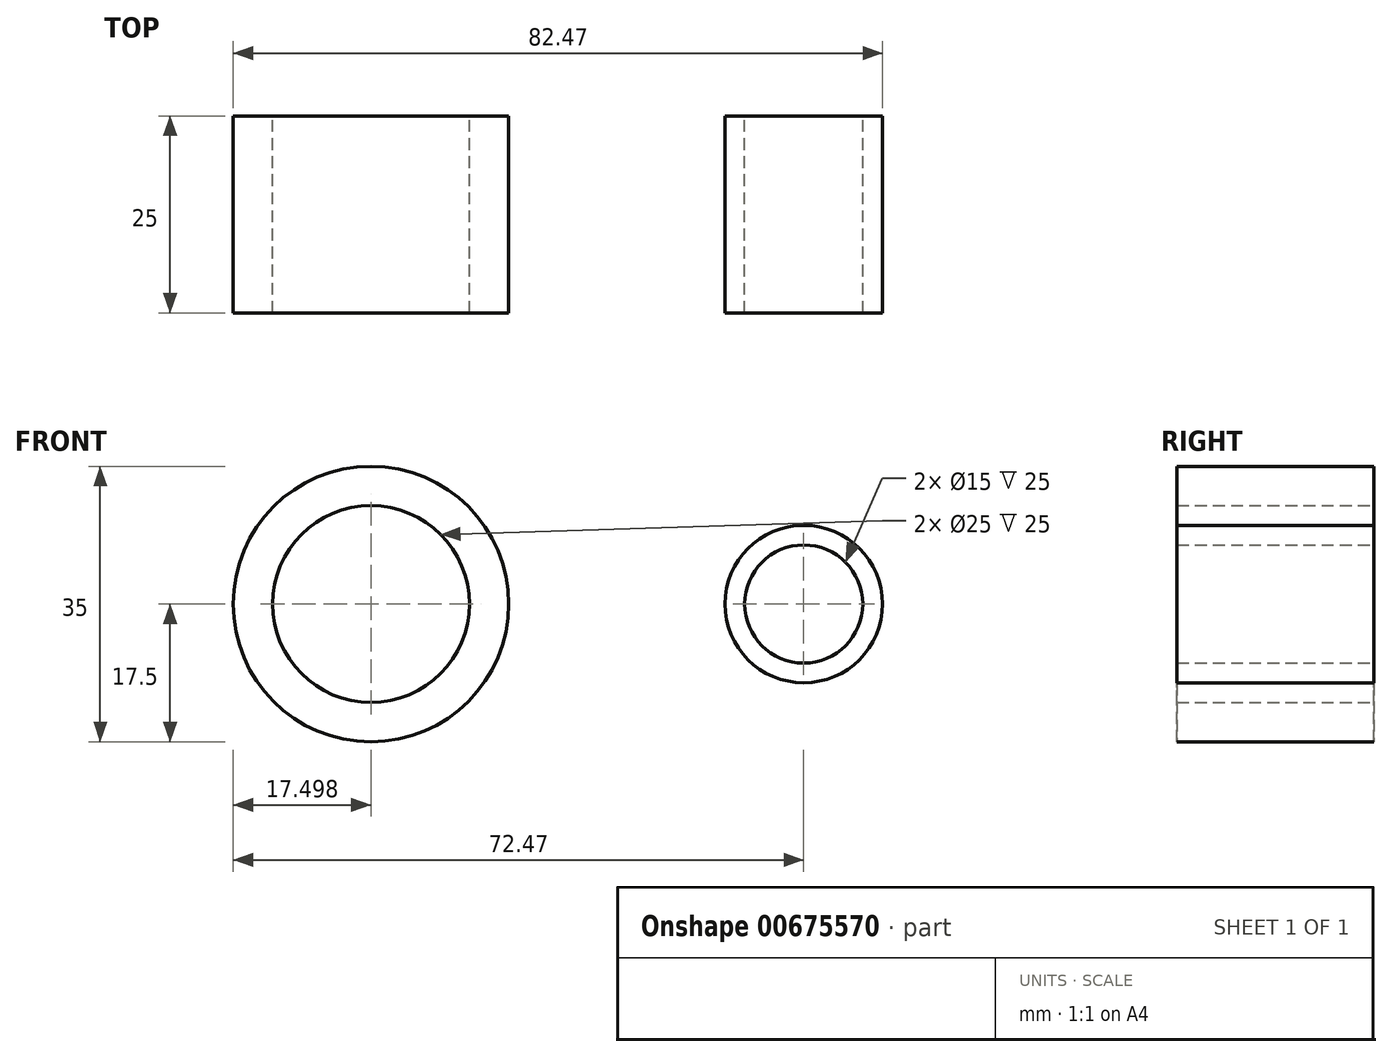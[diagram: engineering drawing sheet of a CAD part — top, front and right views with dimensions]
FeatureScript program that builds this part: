
annotation { "Feature Type Name" : "Feature", "Feature Type Description" : "" }
export const myFeature = defineFeature(function(context is Context, id is Id, definition is map)
    precondition{}
    {
        {
            var Q0;
            Q0=qCreatedBy(makeId("Front.planeOp"),FACE);
            var sketch = newSketch(context, id + "F0", { "sketchPlane" : qUnion([Q0])});
            skCircle(sketch, "E0", {"center": v(-54.97, 0) * mm, "radius": 12.5 * mm});
            skCircle(sketch, "E1", {"center": v(-54.97, 0) * mm, "radius": 17.5 * mm});
            skCircle(sketch, "E2", {"center": v(0, 0) * mm, "radius": 7.5 * mm});
            skCircle(sketch, "E3", {"center": v(0, 0) * mm, "radius": 10 * mm});
            skLineSegment(sketch, "E4", {"start": v(-54.97, 17.5) * mm, "end": v(0, 10.1) * mm});
            skLineSegment(sketch, "E5", {"start": v(-54.97, -17.5) * mm, "end": v(0, -10.1) * mm});
            skSolve(sketch);
        }
        {
            var Q0;
            Q0 = qSketchRegion(id + "F0", true);
            extrude(context, id + "F1", {"entities" : qUnion([Q0]), "depth" : 25 * mm, "offsetDistance" : 25 * mm});
        }
        {
            var Q0;
            Q0 = qSketchRegion(id + "F0", true);
            extrude(context, id + "F2", {"entities" : qUnion([Q0]), "depth" : 25 * mm, "offsetDistance" : 25 * mm});
        }
    });
